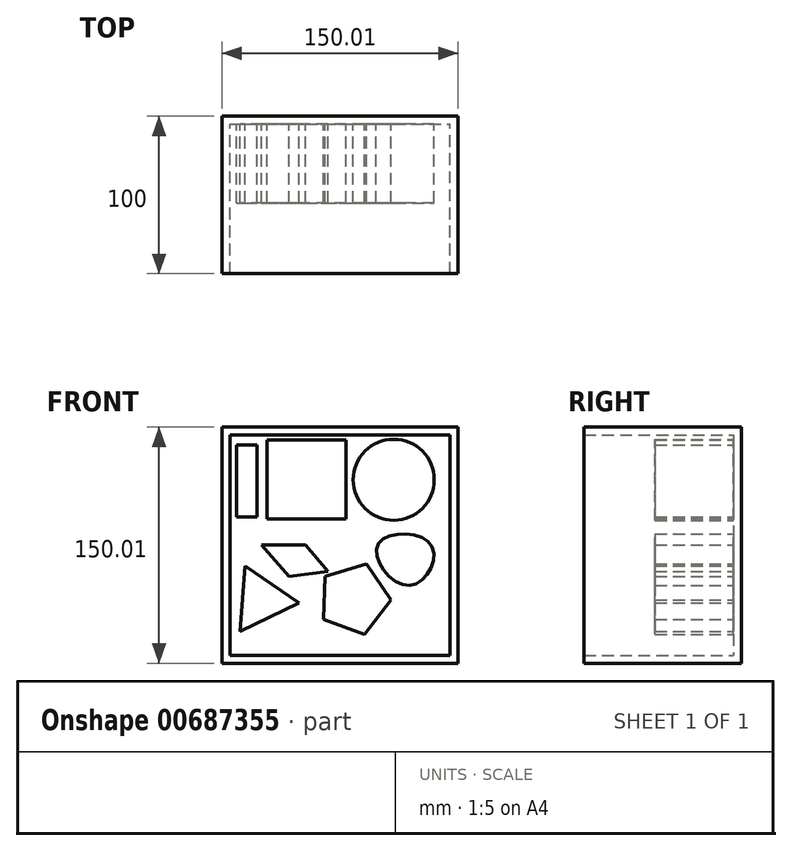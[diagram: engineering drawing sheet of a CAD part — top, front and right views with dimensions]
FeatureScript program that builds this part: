
annotation { "Feature Type Name" : "Feature", "Feature Type Description" : "" }
export const myFeature = defineFeature(function(context is Context, id is Id, definition is map)
    precondition{}
    {
        {
            var Q0;
            Q0=qCreatedBy(makeId("Front.planeOp"),FACE);
            var sketch = newSketch(context, id + "F0", { "sketchPlane" : qUnion([Q0])});
            skLineSegment(sketch, "E0.bottom", {"start": v(-74.88, 74.76) * mm, "end": v(75.13, 74.76) * mm});
            skLineSegment(sketch, "E0.top", {"start": v(-74.88, -75.25) * mm, "end": v(75.13, -75.25) * mm});
            skLineSegment(sketch, "E0.left", {"start": v(-74.88, 74.76) * mm, "end": v(-74.88, -75.25) * mm});
            skLineSegment(sketch, "E0.right", {"start": v(75.13, 74.76) * mm, "end": v(75.13, -75.25) * mm});
            skSolve(sketch);
        }
        {
            var Q0;
            Q0 = qSketchRegion(id + "F0", true);
            extrude(context, id + "F1", {"entities" : qUnion([Q0]), "depth" : 50 * mm, "offsetDistance" : 25 * mm});
        }
        {
            var Q0;
            Q0=makeQuery(id+"F1.opExtrude","CAP_FACE",FACE,{"disambiguationData":[OSD([sQuery(id+"F0.wireOp",EDGE,"E0.bottom"),sQuery(id+"F0.wireOp",EDGE,"E0.top"),sQuery(id+"F0.wireOp",EDGE,"E0.left"),sQuery(id+"F0.wireOp",EDGE,"E0.right")])],"isStart":true});
            extrude(context, id + "F2", {"entities" : qUnion([Q0]), "operationType" : NewBodyOperationType.ADD, "depth" : 50 * mm, "offsetDistance" : 25 * mm});
        }
        {
            var Q0;
            Q0=makeQuery(id+"F1.opExtrude","CAP_FACE",FACE,{"disambiguationData":[OSD([sQuery(id+"F0.wireOp",EDGE,"E0.bottom"),sQuery(id+"F0.wireOp",EDGE,"E0.top"),sQuery(id+"F0.wireOp",EDGE,"E0.left"),sQuery(id+"F0.wireOp",EDGE,"E0.right")])],"isStart":false});
            shell(context, id + "F3", {"entities" : qUnion([Q0]), "thickness" : 5 * mm});
        }
        {
            var Q0;
            Q0=makeQuery(id+"F3.opShell","OFFSET_FACE",FACE,{"disambiguationData":[OSD([sQuery(id+"F0.wireOp",EDGE,"E0.bottom"),sQuery(id+"F0.wireOp",EDGE,"E0.top"),sQuery(id+"F0.wireOp",EDGE,"E0.left"),sQuery(id+"F0.wireOp",EDGE,"E0.right")])]});
            var sketch = newSketch(context, id + "F4", { "sketchPlane" : qUnion([Q0])});
            skLineSegment(sketch, "E1.bottom", {"start": v(-46.4, 66.54) * mm, "end": v(3.93, 66.54) * mm});
            skLineSegment(sketch, "E1.top", {"start": v(-46.4, 16.45) * mm, "end": v(3.93, 16.45) * mm});
            skLineSegment(sketch, "E1.left", {"start": v(-46.4, 66.54) * mm, "end": v(-46.4, 16.45) * mm});
            skLineSegment(sketch, "E1.right", {"start": v(3.93, 66.54) * mm, "end": v(3.93, 16.45) * mm});
            skSolve(sketch);
        }
        {
            var Q0;
            Q0 = qSketchRegion(id + "F4", true);
            extrude(context, id + "F5", {"entities" : qUnion([Q0]), "operationType" : NewBodyOperationType.ADD, "depth" : 50 * mm, "offsetDistance" : 25 * mm});
        }
        {
            var Q0;
            Q0=makeQuery(id+"F3.opShell","OFFSET_FACE",FACE,{"disambiguationData":[OSD([sQuery(id+"F0.wireOp",EDGE,"E0.bottom"),sQuery(id+"F0.wireOp",EDGE,"E0.top"),sQuery(id+"F0.wireOp",EDGE,"E0.left"),sQuery(id+"F0.wireOp",EDGE,"E0.right")])]});
            var sketch = newSketch(context, id + "F6", { "sketchPlane" : qUnion([Q0])});
            skCircle(sketch, "E2", {"center": v(34.23, 41.33) * mm, "radius": 25.7 * mm});
            skSolve(sketch);
        }
        {
            var Q0;
            Q0 = qSketchRegion(id + "F6", true);
            extrude(context, id + "F7", {"entities" : qUnion([Q0]), "operationType" : NewBodyOperationType.ADD, "depth" : 50 * mm, "offsetDistance" : 25 * mm});
        }
        {
            var Q0;
            Q0=makeQuery(id+"F3.opShell","OFFSET_FACE",FACE,{"disambiguationData":[OSD([sQuery(id+"F0.wireOp",EDGE,"E0.bottom"),sQuery(id+"F0.wireOp",EDGE,"E0.top"),sQuery(id+"F0.wireOp",EDGE,"E0.left"),sQuery(id+"F0.wireOp",EDGE,"E0.right")])]});
            var sketch = newSketch(context, id + "F8", { "sketchPlane" : qUnion([Q0])});
            skCircle(sketch, "E3.cCircle", {"center": v(-49.78, -35.09) * mm, "radius": 12.01 * mm, "construction": true});
            skLineSegment(sketch, "E3.0", {"start": v(-60.19, -13.43) * mm, "end": v(-25.82, -36.9) * mm});
            skLineSegment(sketch, "E3.1", {"start": v(-25.82, -36.9) * mm, "end": v(-63.33, -54.93) * mm});
            skLineSegment(sketch, "E3.2", {"start": v(-63.33, -54.93) * mm, "end": v(-60.19, -13.43) * mm});
            skPoint(sketch, "E3.0.midPoint", {"position": v(-43, -25.17) * mm});
            skSolve(sketch);
        }
        {
            var Q0;
            Q0 = qSketchRegion(id + "F8", true);
            extrude(context, id + "F9", {"entities" : qUnion([Q0]), "operationType" : NewBodyOperationType.ADD, "depth" : 50 * mm, "offsetDistance" : 25 * mm});
        }
        {
            var Q0;
            Q0=makeQuery(id+"F3.opShell","OFFSET_FACE",FACE,{"disambiguationData":[OSD([sQuery(id+"F0.wireOp",EDGE,"E0.bottom"),sQuery(id+"F0.wireOp",EDGE,"E0.top"),sQuery(id+"F0.wireOp",EDGE,"E0.left"),sQuery(id+"F0.wireOp",EDGE,"E0.right")])]});
            var sketch = newSketch(context, id + "F10", { "sketchPlane" : qUnion([Q0])});
            skCircle(sketch, "E4.cCircle", {"center": v(9.02, -34.36) * mm, "radius": 19 * mm, "construction": true});
            skLineSegment(sketch, "E4.0", {"start": v(17, -12.29) * mm, "end": v(32.48, -35.14) * mm});
            skLineSegment(sketch, "E4.1", {"start": v(32.48, -35.14) * mm, "end": v(15.52, -56.92) * mm});
            skLineSegment(sketch, "E4.2", {"start": v(15.52, -56.92) * mm, "end": v(-10.42, -47.52) * mm});
            skLineSegment(sketch, "E4.3", {"start": v(-10.42, -47.52) * mm, "end": v(-9.5, -19.94) * mm});
            skLineSegment(sketch, "E4.4", {"start": v(-9.5, -19.94) * mm, "end": v(17, -12.29) * mm});
            skPoint(sketch, "E4.0.midPoint", {"position": v(24.74, -23.72) * mm});
            skSolve(sketch);
        }
        {
            var Q0;
            Q0 = qSketchRegion(id + "F10", true);
            extrude(context, id + "F11", {"entities" : qUnion([Q0]), "operationType" : NewBodyOperationType.ADD, "depth" : 50 * mm, "offsetDistance" : 25 * mm});
        }
        {
            var Q0;
            Q0=makeQuery(id+"F3.opShell","OFFSET_FACE",FACE,{"disambiguationData":[OSD([sQuery(id+"F0.wireOp",EDGE,"E0.bottom"),sQuery(id+"F0.wireOp",EDGE,"E0.top"),sQuery(id+"F0.wireOp",EDGE,"E0.left"),sQuery(id+"F0.wireOp",EDGE,"E0.right")])]});
            var sketch = newSketch(context, id + "F12", { "sketchPlane" : qUnion([Q0])});
            skLineSegment(sketch, "E5.bottom", {"start": v(-65.73, 63.46) * mm, "end": v(-52.44, 63.46) * mm});
            skLineSegment(sketch, "E5.top", {"start": v(-65.73, 17.71) * mm, "end": v(-52.44, 17.71) * mm});
            skLineSegment(sketch, "E5.left", {"start": v(-65.73, 63.46) * mm, "end": v(-65.73, 17.71) * mm});
            skLineSegment(sketch, "E5.right", {"start": v(-52.44, 63.46) * mm, "end": v(-52.44, 17.71) * mm});
            skSolve(sketch);
        }
        {
            var Q0;
            Q0 = qSketchRegion(id + "F12", true);
            extrude(context, id + "F13", {"entities" : qUnion([Q0]), "operationType" : NewBodyOperationType.ADD, "depth" : 50 * mm, "offsetDistance" : 25 * mm});
        }
        {
            var Q0;
            Q0=makeQuery(id+"F3.opShell","OFFSET_FACE",FACE,{"disambiguationData":[OSD([sQuery(id+"F0.wireOp",EDGE,"E0.bottom"),sQuery(id+"F0.wireOp",EDGE,"E0.top"),sQuery(id+"F0.wireOp",EDGE,"E0.left"),sQuery(id+"F0.wireOp",EDGE,"E0.right")])]});
            var sketch = newSketch(context, id + "F14", { "sketchPlane" : qUnion([Q0])});
            skLineSegment(sketch, "E6", {"start": v(-32.36, -20.09) * mm, "end": v(-49.78, 0) * mm});
            skLineSegment(sketch, "E7", {"start": v(-49.78, 0) * mm, "end": v(-21.71, 0) * mm});
            skLineSegment(sketch, "E8", {"start": v(-21.71, 0) * mm, "end": v(-7.44, -16.94) * mm});
            skLineSegment(sketch, "E9", {"start": v(-7.44, -16.94) * mm, "end": v(-32.36, -20.09) * mm});
            skSolve(sketch);
        }
        {
            var Q0;
            Q0 = qSketchRegion(id + "F14", true);
            extrude(context, id + "F15", {"entities" : qUnion([Q0]), "operationType" : NewBodyOperationType.ADD, "depth" : 50 * mm, "offsetDistance" : 25 * mm});
        }
        {
            var Q0;
            Q0=makeQuery(id+"F3.opShell","OFFSET_FACE",FACE,{"disambiguationData":[OSD([sQuery(id+"F0.wireOp",EDGE,"E0.bottom"),sQuery(id+"F0.wireOp",EDGE,"E0.top"),sQuery(id+"F0.wireOp",EDGE,"E0.left"),sQuery(id+"F0.wireOp",EDGE,"E0.right")])]});
            var sketch = newSketch(context, id + "F16", { "sketchPlane" : qUnion([Q0])});
            skFitSpline(sketch, "E10", {"points": [v(44.1, -25.9) * mm, v(24.02, 0) * mm, v(57.9, 0) * mm, v(44.1, -25.9) * mm]});
            skSolve(sketch);
        }
        {
            var Q0;
            Q0 = qSketchRegion(id + "F16", true);
            extrude(context, id + "F17", {"entities" : qUnion([Q0]), "operationType" : NewBodyOperationType.ADD, "depth" : 50 * mm, "offsetDistance" : 25 * mm});
        }
    });
